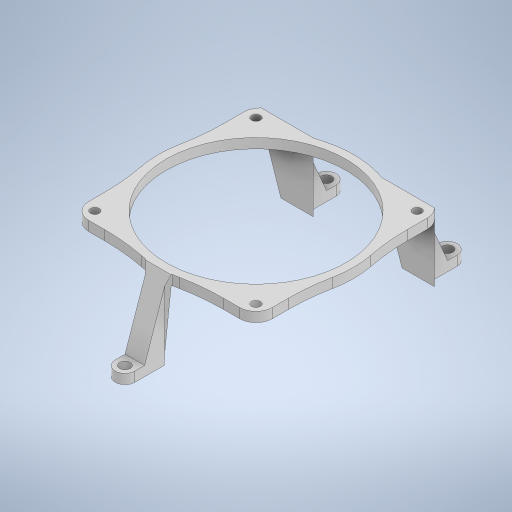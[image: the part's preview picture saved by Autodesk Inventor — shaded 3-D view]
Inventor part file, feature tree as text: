
AUTODESK INVENTOR PART (.ipt)
format: ipt  version: 2023 (Build 270158030, 158C)  size: 406,528 bytes
history: native  units: in
note: dims shown in document units (in); Inventor stores cm internally (conversion verified against a paired STEP export)
features: sketch x8, extrude x6, plane x2, hole x2, chamfer x2, fillet x2, mirror x1
ambient origin geometry x8: Origin, YZ Plane, XZ Plane, XY Plane, X Axis, Y Axis, Z Axis, Center Point
bodies: Solid1 (feature_tree)
feature tree (23):
  plane  "Work Plane1"
  extrude  "Extrusion1"  Depth=1.378in
  plane  "Work Plane2"
  extrude  "Extrusion2"  Depth=3.248in
  extrude  "Extrusion3"  Depth=0.7874in
  hole  "Hole1"  [1 undecoded]
  mirror  "Mirror1"
  extrude  "Extrusion4"  Depth=0.1969in
  extrude  "Extrusion5"  Depth=0.5906in
  extrude  "Extrusion6"  Depth=0.1969in
  hole  "Hole2"  [1 undecoded]
  chamfer  "Chamfer1"  Distance=4.1412in
  fillet  "Fillet1"  Radius=0.3287in
  fillet  "Fillet2"  Radius=0.3287in
  chamfer  "Chamfer2"  Distance=0.1969in
  sketch  "Sketch1"  dims[d0=1.378in d1=3.622in]
  sketch  "Sketch2"  dims[d2=0.1772in d3=3.248in]
  sketch  "Sketch3"  dims[d4=3.248in d5=0.7874in d7=3.248in d8=0.7874in d10=3.248in]
  sketch  "Sketch4"  dims[d13=3.7008in d14=3.7008in]
  sketch  "Sketch6"  dims[d15=0.1969in d16=0.0in d17=3.937in]
  sketch  "Sketch7"  dims[d18=-0.6299in d19=0.5906in]
  sketch  "Sketch8"  dims[d20=0.1969in d21=0.1969in]
  sketch  "Sketch9"  dims[d22=1.378in d23=0.3937in d24=0.0in d25=4.1412in d26=0.3287in d27=0.3287in d28=0.0787in d29=45.0deg d30=0.1969in d31=0.0in d32=0.2165in d33=0.2362in d34=0.3937in d35=0.2244in d36=90.0deg d37=0.3465in d38=0.8108in d39=0.1969in d40=0.5906in d41=0.1969in d43=1.378in d44=0.3937in d45=0.0in d46=0.3937in d47=0.0in d48=0.0in d49=0.0in d50=0.2165in d51=0.2362in d52=0.3937in d53=0.2244in d54=90.0deg d55=0.315in d56=0.8108in d57=0.0787in d58=0.0787in d59=45.0deg]
note: 2 required parameter values undecoded (feature->parameter linkage not recoverable at this tier; creation-order binding heuristic only, values carry confidence <= 0.55)
